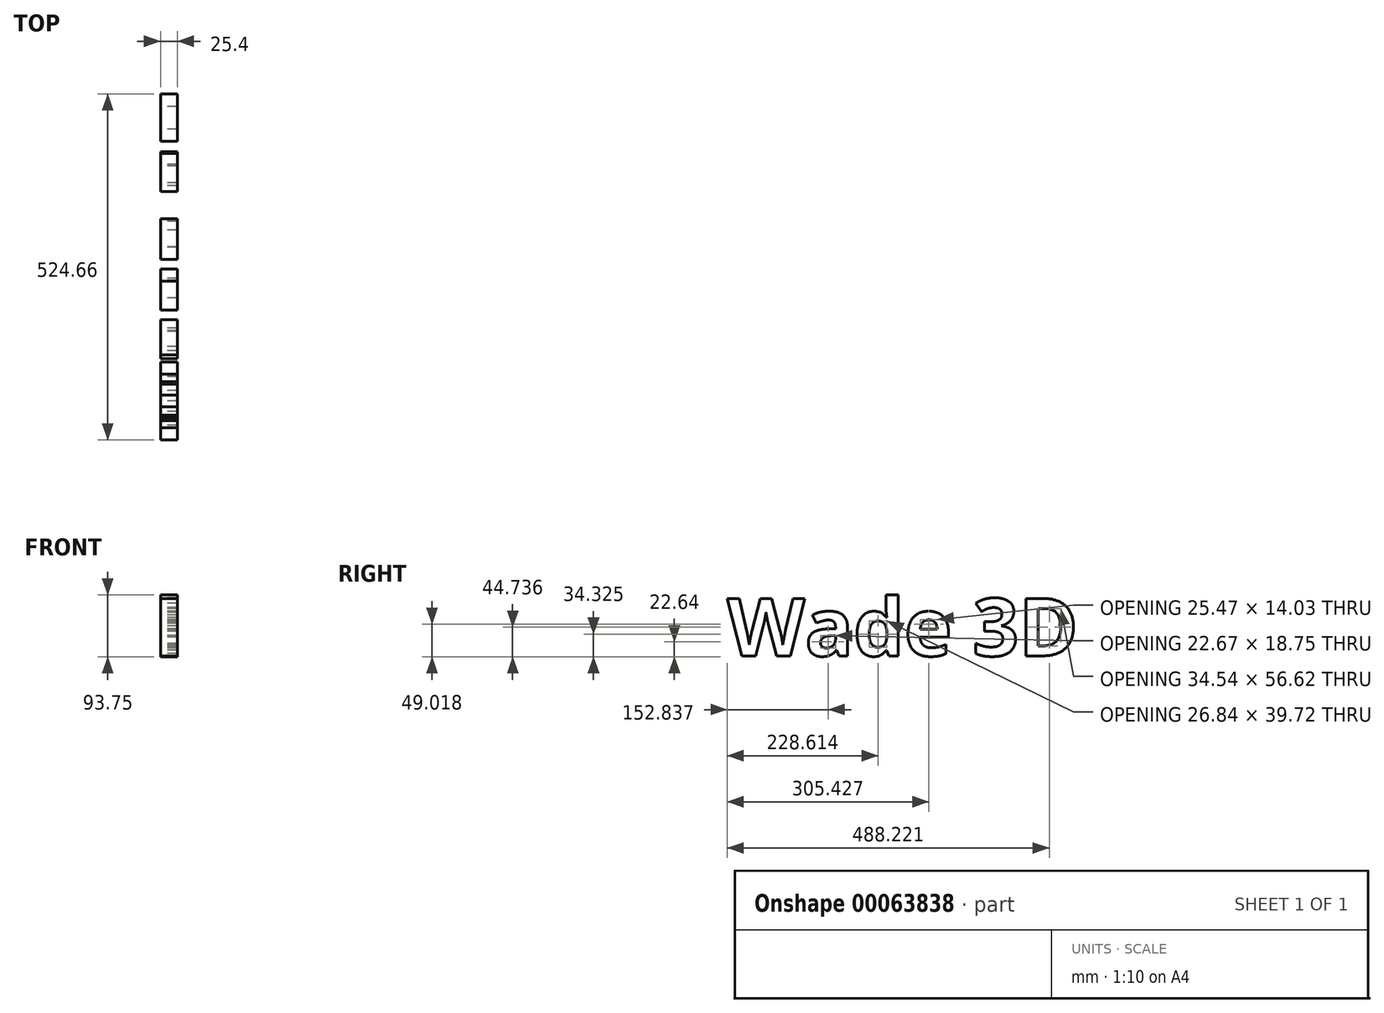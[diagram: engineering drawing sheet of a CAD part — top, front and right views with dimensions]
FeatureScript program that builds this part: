
annotation { "Feature Type Name" : "Feature", "Feature Type Description" : "" }
export const myFeature = defineFeature(function(context is Context, id is Id, definition is map)
    precondition{}
    {
        {
            var Q0;
            Q0=qCreatedBy(makeId("Right.planeOp"),FACE);
            var sketch = newSketch(context, id + "F0", { "sketchPlane" : qUnion([Q0])});
            skText(sketch, "E0", { "text": "Wade 3D", "fontName": "OpenSans-Bold.ttf"});
            const initialGuessF0  = {"E0": [-0.18348, -0.00407, 1, 0, 0.0877]};
            skSetInitialGuess(sketch, initialGuessF0);
            skSolve(sketch);
        }
        {
            var Q0;
            Q0 = qSketchRegion(id + "F0", true);
            extrude(context, id + "F1", {"entities" : qUnion([Q0]), "depth" : 25.4 * mm});
        }
    });
